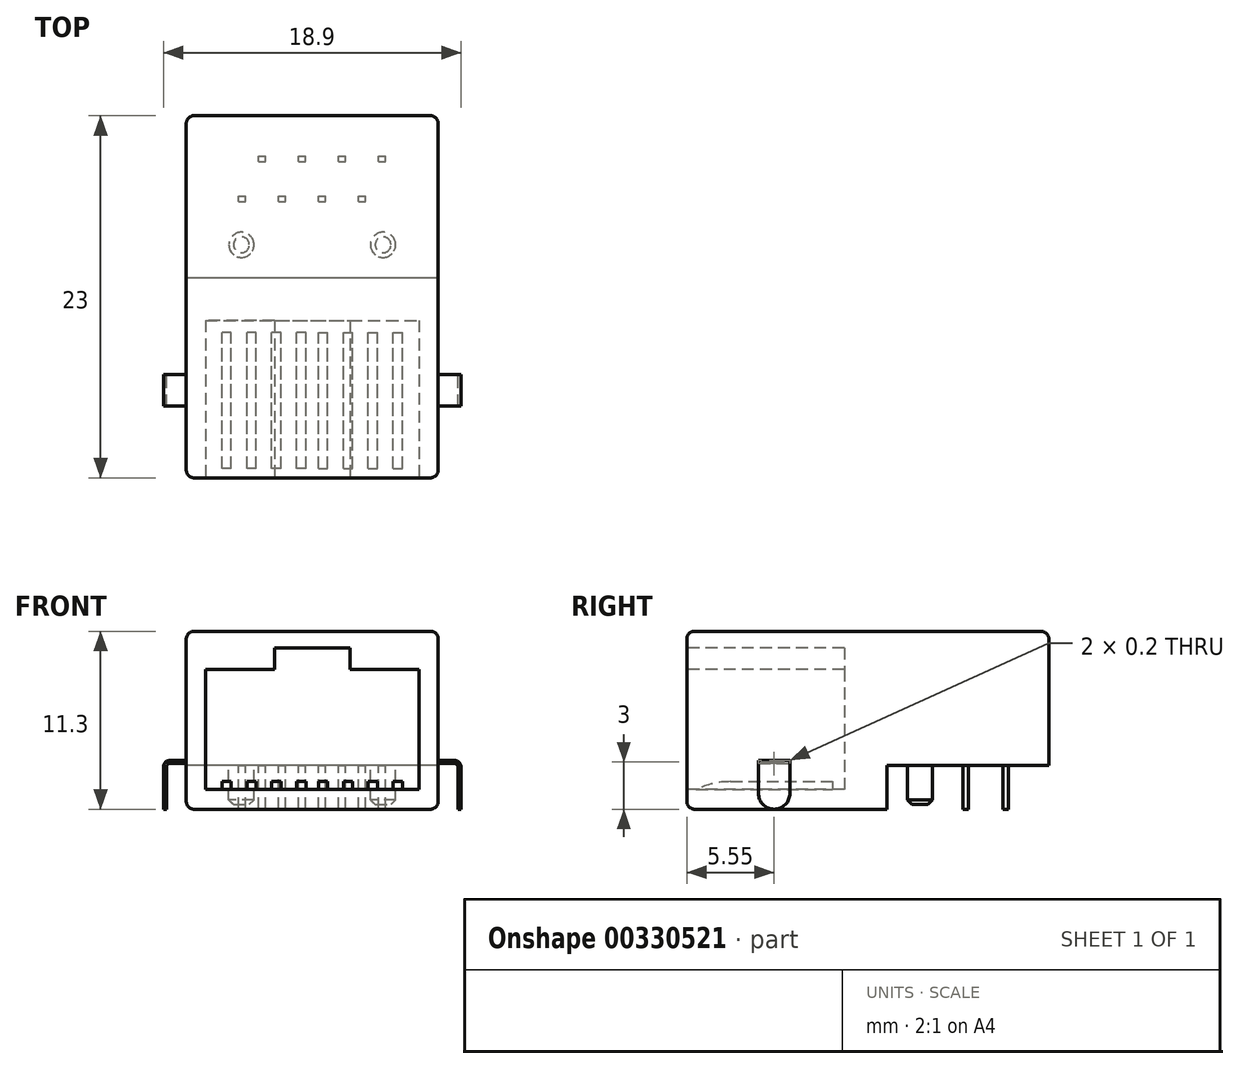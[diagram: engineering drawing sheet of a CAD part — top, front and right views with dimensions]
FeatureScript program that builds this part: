
annotation { "Feature Type Name" : "Feature", "Feature Type Description" : "" }
export const myFeature = defineFeature(function(context is Context, id is Id, definition is map)
    precondition{}
    {
        {
            var Q0;
            Q0=qCreatedBy(makeId("Top.planeOp"),FACE);
            var sketch = newSketch(context, id + "F0", { "sketchPlane" : qUnion([Q0])});
            skLineSegment(sketch, "E0.bottom", {"start": v(8, -11.5) * mm, "end": v(-8, -11.5) * mm});
            skLineSegment(sketch, "E0.top", {"start": v(8, 11.5) * mm, "end": v(-8, 11.5) * mm});
            skLineSegment(sketch, "E0.left", {"start": v(8, -11.5) * mm, "end": v(8, 11.5) * mm});
            skLineSegment(sketch, "E0.right", {"start": v(-8, -11.5) * mm, "end": v(-8, 11.5) * mm});
            skPoint(sketch, "E0.middle", {"position": v(0, 0) * mm});
            skSolve(sketch);
        }
        {
            var Q0;
            Q0 = qSketchRegion(id + "F0", true);
            extrude(context, id + "F1", {"entities" : qUnion([Q0]), "depth" : 8.5 * mm, "offsetDistance" : 25 * mm});
        }
        {
            var Q0;
            Q0=makeQuery(id+"F1.opExtrude","CAP_FACE",FACE,{"disambiguationData":[OSD([sQuery(id+"F0.wireOp",EDGE,"E0.bottom"),sQuery(id+"F0.wireOp",EDGE,"E0.top"),sQuery(id+"F0.wireOp",EDGE,"E0.left"),sQuery(id+"F0.wireOp",EDGE,"E0.right")])],"isStart":true});
            var sketch = newSketch(context, id + "F2", { "sketchPlane" : qUnion([Q0])});
            skLineSegment(sketch, "E1.bottom", {"start": v(8, 11.5) * mm, "end": v(-8, 11.5) * mm});
            skLineSegment(sketch, "E1.top", {"start": v(8, -1.2) * mm, "end": v(-8, -1.2) * mm});
            skLineSegment(sketch, "E1.left", {"start": v(8, 11.5) * mm, "end": v(8, -1.2) * mm});
            skLineSegment(sketch, "E1.right", {"start": v(-8, 11.5) * mm, "end": v(-8, -1.2) * mm});
            skSolve(sketch);
        }
        {
            var Q0;
            Q0=makeQuery(id+"F2.imprint","IMPRINT",FACE,{"disambiguationData":[TD([[makeQuery(id+"F2.imprint","IMPRINT",EDGE,{"derivedFrom":sQuery(id+"F2.wireOp",EDGE,"E1.bottom")}),1.0]])]});
            extrude(context, id + "F3", {"entities" : qUnion([Q0]), "operationType" : NewBodyOperationType.ADD, "depth" : (11.3 - 8.5) * mm, "offsetDistance" : 25 * mm});
        }
        {
            var Q0;
            Q0=makeQuery(id+"F3.boolean.opBoolean","MERGE",EDGE,{"derivedFrom":[makeQuery(id+"F1.opExtrude","SWEPT_EDGE",EDGE,{"disambiguationData":[OSD([sQuery(id+"F0.wireOp",EDGE,"E0.bottom"),sQuery(id+"F0.wireOp",EDGE,"E0.right")])]}),makeQuery(id+"F3.opExtrude","SWEPT_EDGE",EDGE,{"disambiguationData":[OSD([sQuery(id+"F2.wireOp",EDGE,"E1.bottom"),sQuery(id+"F2.wireOp",EDGE,"E1.right")])]})]});
            var Q1;
            Q1=makeQuery(id+"F3.boolean.opBoolean","MERGE",EDGE,{"derivedFrom":[makeQuery(id+"F1.opExtrude","SWEPT_EDGE",EDGE,{"disambiguationData":[OSD([sQuery(id+"F0.wireOp",EDGE,"E0.bottom"),sQuery(id+"F0.wireOp",EDGE,"E0.left")])]}),makeQuery(id+"F3.opExtrude","SWEPT_EDGE",EDGE,{"disambiguationData":[OSD([sQuery(id+"F2.wireOp",EDGE,"E1.bottom"),sQuery(id+"F2.wireOp",EDGE,"E1.left")])]})]});
            var Q2;
            Q2=makeQuery(id+"F1.opExtrude","SWEPT_EDGE",EDGE,{"disambiguationData":[OSD([sQuery(id+"F0.wireOp",EDGE,"E0.top"),sQuery(id+"F0.wireOp",EDGE,"E0.left")])]});
            var Q3;
            Q3=makeQuery(id+"F1.opExtrude","SWEPT_EDGE",EDGE,{"disambiguationData":[OSD([sQuery(id+"F0.wireOp",EDGE,"E0.top"),sQuery(id+"F0.wireOp",EDGE,"E0.right")])]});
            var Q4;
            Q4=makeQuery(id+"F1.opExtrude","CAP_EDGE",EDGE,{"disambiguationData":[OSD([sQuery(id+"F0.wireOp",EDGE,"E0.bottom")])],"isStart":false});
            var Q5;
            Q5=makeQuery(id+"F1.opExtrude","CAP_EDGE",EDGE,{"disambiguationData":[OSD([sQuery(id+"F0.wireOp",EDGE,"E0.right")])],"isStart":false});
            var Q6;
            Q6=makeQuery(id+"F1.opExtrude","CAP_EDGE",EDGE,{"disambiguationData":[OSD([sQuery(id+"F0.wireOp",EDGE,"E0.top")])],"isStart":false});
            var Q7;
            Q7=makeQuery(id+"F1.opExtrude","CAP_EDGE",EDGE,{"disambiguationData":[OSD([sQuery(id+"F0.wireOp",EDGE,"E0.left")])],"isStart":false});
            var Q8;
            Q8=makeQuery(id+"F3.opExtrude","CAP_EDGE",EDGE,{"disambiguationData":[OSD([sQuery(id+"F2.wireOp",EDGE,"E1.bottom")])],"isStart":false});
            var Q9;
            Q9=makeQuery(id+"F3.opExtrude","CAP_EDGE",EDGE,{"disambiguationData":[OSD([sQuery(id+"F2.wireOp",EDGE,"E1.right")])],"isStart":false});
            var Q10;
            Q10=makeQuery(id+"F3.opExtrude","CAP_EDGE",EDGE,{"disambiguationData":[OSD([sQuery(id+"F2.wireOp",EDGE,"E1.left")])],"isStart":false});
            fillet(context, id + "F4", {"entities" : qUnion([Q0, Q1, Q2, Q3, Q4, Q5, Q6, Q7, Q8, Q9, Q10]), "radius" : .5 * mm, "tangentPropagation" : true, "allowEdgeOverflow" : false});
        }
        {
            var Q0;
            Q0=makeQuery(id+"F1.opExtrude","CAP_FACE",FACE,{"disambiguationData":[OSD([sQuery(id+"F0.wireOp",EDGE,"E0.bottom"),sQuery(id+"F0.wireOp",EDGE,"E0.top"),sQuery(id+"F0.wireOp",EDGE,"E0.left"),sQuery(id+"F0.wireOp",EDGE,"E0.right")])],"isStart":true});
            var sketch = newSketch(context, id + "F5", { "sketchPlane" : qUnion([Q0])});
            skCircle(sketch, "E2", {"center": v(4.5, -3.3) * mm, "radius": 0.8 * mm});
            skLineSegment(sketch, "E3", {"start": v(0, -11.5) * mm, "end": v(0, 9.2) * mm, "construction": true});
            skCircle(sketch, "E4.MirrorC", {"center": v(-4.5, -3.3) * mm, "radius": 0.8 * mm});
            skSolve(sketch);
        }
        {
            var Q0;
            Q0 = qSketchRegion(id + "F5", true);
            extrude(context, id + "F6", {"entities" : qUnion([Q0]), "operationType" : NewBodyOperationType.ADD, "depth" : 2.5 * mm, "offsetDistance" : 25 * mm});
        }
        {
            var Q0;
            Q0=makeQuery(id+"F6.opExtrude","CAP_EDGE",EDGE,{"disambiguationData":[OSD([sQuery(id+"F5.wireOp",EDGE,"E2")])],"isStart":false});
            var Q1;
            Q1=makeQuery(id+"F6.opExtrude","CAP_EDGE",EDGE,{"disambiguationData":[OSD([sQuery(id+"F5.wireOp",EDGE,"E4.MirrorC")])],"isStart":false});
            chamfer(context, id + "F7", {"entities" : qUnion([Q0, Q1]), "width" : .3 * mm, "tangentPropagation" : true});
        }
        {
            var Q0;
            Q0=makeQuery(id+"F3.boolean.opBoolean","MERGE",FACE,{"derivedFrom":[makeQuery(id+"F1.opExtrude","SWEPT_FACE",FACE,{"disambiguationData":[OSD([sQuery(id+"F0.wireOp",EDGE,"E0.bottom")])]}),makeQuery(id+"F3.opExtrude","SWEPT_FACE",FACE,{"disambiguationData":[OSD([sQuery(id+"F2.wireOp",EDGE,"E1.bottom")])]})]});
            var sketch = newSketch(context, id + "F8", { "sketchPlane" : qUnion([Q0])});
            skLineSegment(sketch, "E5", {"start": v(0, 8) * mm, "end": v(0, -2.3) * mm, "construction": true});
            skLineSegment(sketch, "E6", {"start": v(0, 7.46) * mm, "end": v(2.4, 7.46) * mm});
            skLineSegment(sketch, "E7", {"start": v(2.4, 7.46) * mm, "end": v(2.4, 6.09) * mm});
            skLineSegment(sketch, "E8", {"start": v(2.4, 6.09) * mm, "end": v(6.78, 6.09) * mm});
            skLineSegment(sketch, "E9", {"start": v(6.78, 6.09) * mm, "end": v(6.78, -1.54) * mm});
            skLineSegment(sketch, "E10", {"start": v(6.78, -1.54) * mm, "end": v(0, -1.54) * mm});
            skLineSegment(sketch, "E11.MirrorCS", {"start": v(-6.78, -1.54) * mm, "end": v(0, -1.54) * mm});
            skLineSegment(sketch, "E12.MirrorCS", {"start": v(-6.78, 6.09) * mm, "end": v(-6.78, -1.54) * mm});
            skLineSegment(sketch, "E13.MirrorCS", {"start": v(-2.4, 6.09) * mm, "end": v(-6.78, 6.09) * mm});
            skLineSegment(sketch, "E14.MirrorCS", {"start": v(0, 7.46) * mm, "end": v(-2.4, 7.46) * mm});
            skLineSegment(sketch, "E15.MirrorCS", {"start": v(-2.4, 7.46) * mm, "end": v(-2.4, 6.09) * mm});
            skSolve(sketch);
        }
        {
            var Q0;
            Q0 = qSketchRegion(id + "F8", true);
            extrude(context, id + "F9", {"entities" : qUnion([Q0]), "operationType" : NewBodyOperationType.REMOVE, "oppositeDirection" : true, "depth" : 10 * mm, "offsetDistance" : 25 * mm});
        }
        {
            var Q0;
            Q0=makeQuery(id+"F9.boolean.opBoolean","COPY",FACE,{"derivedFrom":makeQuery(id+"F9.opExtrude","SWEPT_FACE",FACE,{"disambiguationData":[OSD([sQuery(id+"F8.wireOp",EDGE,"E10"),sQuery(id+"F8.wireOp",EDGE,"E11.MirrorCS")])]})});
            var sketch = newSketch(context, id + "F10", { "sketchPlane" : qUnion([Q0])});
            skLineSegment(sketch, "E16", {"start": v(0, -11.5) * mm, "end": v(0, -1.5) * mm, "construction": true});
            skLineSegment(sketch, "E17.bottom", {"start": v(0.4, -10.9) * mm, "end": v(0.99, -10.9) * mm});
            skLineSegment(sketch, "E17.top", {"start": v(0.4, -2.26) * mm, "end": v(0.99, -2.26) * mm});
            skLineSegment(sketch, "E17.left", {"start": v(0.4, -10.9) * mm, "end": v(0.4, -2.26) * mm});
            skLineSegment(sketch, "E17.right", {"start": v(0.99, -10.9) * mm, "end": v(0.99, -2.26) * mm});
            skLineSegment(sketch, "E18.1.0.0", {"start": v(1.98, -10.9) * mm, "end": v(2.57, -10.9) * mm});
            skLineSegment(sketch, "E18.1.0.1", {"start": v(1.98, -2.26) * mm, "end": v(2.57, -2.26) * mm});
            skLineSegment(sketch, "E18.1.0.2", {"start": v(1.98, -10.9) * mm, "end": v(1.98, -2.26) * mm});
            skLineSegment(sketch, "E18.1.0.3", {"start": v(2.57, -10.9) * mm, "end": v(2.57, -2.26) * mm});
            skLineSegment(sketch, "E18.2.0.0", {"start": v(3.56, -10.9) * mm, "end": v(4.15, -10.9) * mm});
            skLineSegment(sketch, "E18.2.0.1", {"start": v(3.56, -2.26) * mm, "end": v(4.15, -2.26) * mm});
            skLineSegment(sketch, "E18.2.0.2", {"start": v(3.56, -10.9) * mm, "end": v(3.56, -2.26) * mm});
            skLineSegment(sketch, "E18.2.0.3", {"start": v(4.15, -10.9) * mm, "end": v(4.15, -2.26) * mm});
            skLineSegment(sketch, "E18.3.0.0", {"start": v(5.14, -10.9) * mm, "end": v(5.73, -10.9) * mm});
            skLineSegment(sketch, "E18.3.0.1", {"start": v(5.14, -2.26) * mm, "end": v(5.73, -2.26) * mm});
            skLineSegment(sketch, "E18.3.0.2", {"start": v(5.14, -10.9) * mm, "end": v(5.14, -2.26) * mm});
            skLineSegment(sketch, "E18.3.0.3", {"start": v(5.73, -10.9) * mm, "end": v(5.73, -2.26) * mm});
            skLineSegment(sketch, "E18.direction1", {"start": v(0.4, -10.9) * mm, "end": v(1.98, -10.9) * mm, "construction": true});
            skLineSegment(sketch, "E19.MirrorCS", {"start": v(-0.4, -10.9) * mm, "end": v(-0.99, -10.9) * mm});
            skLineSegment(sketch, "E20.MirrorCS", {"start": v(-4.15, -10.9) * mm, "end": v(-4.15, -2.26) * mm});
            skLineSegment(sketch, "E21.MirrorCS", {"start": v(-3.56, -10.9) * mm, "end": v(-3.56, -2.26) * mm});
            skLineSegment(sketch, "E22.MirrorCS", {"start": v(-3.56, -2.26) * mm, "end": v(-4.15, -2.26) * mm});
            skLineSegment(sketch, "E23.MirrorCS", {"start": v(-3.56, -10.9) * mm, "end": v(-4.15, -10.9) * mm});
            skLineSegment(sketch, "E24.MirrorCS", {"start": v(-2.57, -10.9) * mm, "end": v(-2.57, -2.26) * mm});
            skLineSegment(sketch, "E25.MirrorCS", {"start": v(-1.98, -10.9) * mm, "end": v(-1.98, -2.26) * mm});
            skLineSegment(sketch, "E26.MirrorCS", {"start": v(-1.98, -2.26) * mm, "end": v(-2.57, -2.26) * mm});
            skLineSegment(sketch, "E27.MirrorCS", {"start": v(-1.98, -10.9) * mm, "end": v(-2.57, -10.9) * mm});
            skLineSegment(sketch, "E28.MirrorCS", {"start": v(-0.99, -10.9) * mm, "end": v(-0.99, -2.26) * mm});
            skLineSegment(sketch, "E29.MirrorCS", {"start": v(-0.4, -10.9) * mm, "end": v(-0.4, -2.26) * mm});
            skLineSegment(sketch, "E30.MirrorCS", {"start": v(-0.4, -2.26) * mm, "end": v(-0.99, -2.26) * mm});
            skLineSegment(sketch, "E31.MirrorCS", {"start": v(-5.73, -10.9) * mm, "end": v(-5.73, -2.26) * mm});
            skLineSegment(sketch, "E32.MirrorCS", {"start": v(-5.14, -10.9) * mm, "end": v(-5.14, -2.26) * mm});
            skLineSegment(sketch, "E33.MirrorCS", {"start": v(-5.14, -2.26) * mm, "end": v(-5.73, -2.26) * mm});
            skLineSegment(sketch, "E34.MirrorCS", {"start": v(-0.4, -10.9) * mm, "end": v(-1.98, -10.9) * mm, "construction": true});
            skLineSegment(sketch, "E35.MirrorCS", {"start": v(-5.14, -10.9) * mm, "end": v(-5.73, -10.9) * mm});
            skSolve(sketch);
        }
        {
            var Q0;
            Q0 = qSketchRegion(id + "F10", true);
            extrude(context, id + "F11", {"entities" : qUnion([Q0]), "depth" : .5 * mm, "offsetDistance" : 25 * mm});
        }
        {
            var Q0;
            Q0=makeQuery(id+"F11.opExtrude","CAP_EDGE",EDGE,{"disambiguationData":[OSD([sQuery(id+"F10.wireOp",EDGE,"E35.MirrorCS")])],"isStart":false});
            var Q1;
            Q1=makeQuery(id+"F11.opExtrude","CAP_EDGE",EDGE,{"disambiguationData":[OSD([sQuery(id+"F10.wireOp",EDGE,"E23.MirrorCS")])],"isStart":false});
            var Q2;
            Q2=makeQuery(id+"F11.opExtrude","CAP_EDGE",EDGE,{"disambiguationData":[OSD([sQuery(id+"F10.wireOp",EDGE,"E27.MirrorCS")])],"isStart":false});
            var Q3;
            Q3=makeQuery(id+"F11.opExtrude","CAP_EDGE",EDGE,{"disambiguationData":[OSD([sQuery(id+"F10.wireOp",EDGE,"E19.MirrorCS")])],"isStart":false});
            var Q4;
            Q4=makeQuery(id+"F11.opExtrude","CAP_EDGE",EDGE,{"disambiguationData":[OSD([sQuery(id+"F10.wireOp",EDGE,"E17.bottom")])],"isStart":false});
            var Q5;
            Q5=makeQuery(id+"F11.opExtrude","CAP_EDGE",EDGE,{"disambiguationData":[OSD([sQuery(id+"F10.wireOp",EDGE,"E18.1.0.0")])],"isStart":false});
            var Q6;
            Q6=makeQuery(id+"F11.opExtrude","CAP_EDGE",EDGE,{"disambiguationData":[OSD([sQuery(id+"F10.wireOp",EDGE,"E18.2.0.0")])],"isStart":false});
            var Q7;
            Q7=makeQuery(id+"F11.opExtrude","CAP_EDGE",EDGE,{"disambiguationData":[OSD([sQuery(id+"F10.wireOp",EDGE,"E18.3.0.0")])],"isStart":false});
            fillet(context, id + "F12", {"entities" : qUnion([Q0, Q1, Q2, Q3, Q4, Q5, Q6, Q7]), "radius" : 5 * mm, "tangentPropagation" : true, "allowEdgeOverflow" : false});
        }
        {
            var Q0;
            Q0=makeQuery(id+"F1.opExtrude","CAP_FACE",FACE,{"disambiguationData":[OSD([sQuery(id+"F0.wireOp",EDGE,"E0.bottom"),sQuery(id+"F0.wireOp",EDGE,"E0.top"),sQuery(id+"F0.wireOp",EDGE,"E0.left"),sQuery(id+"F0.wireOp",EDGE,"E0.right")])],"isStart":true});
            var sketch = newSketch(context, id + "F13", { "sketchPlane" : qUnion([Q0])});
            skLineSegment(sketch, "E36", {"start": v(0, -1.2) * mm, "end": v(0, -11.5) * mm, "construction": true});
            skLineSegment(sketch, "E37", {"start": v(6.92, -8.76) * mm, "end": v(-6.94, -8.76) * mm, "construction": true});
            skLineSegment(sketch, "E38", {"start": v(6.71, -6.22) * mm, "end": v(-6.94, -6.22) * mm, "construction": true});
            skLineSegment(sketch, "E39", {"start": v(4.5, -3.3) * mm, "end": v(-4.5, -3.3) * mm, "construction": true});
            skLineSegment(sketch, "E40.bottom", {"start": v(4.22, -8.59) * mm, "end": v(4.67, -8.59) * mm});
            skLineSegment(sketch, "E40.top", {"start": v(4.22, -8.94) * mm, "end": v(4.67, -8.94) * mm});
            skLineSegment(sketch, "E40.left", {"start": v(4.22, -8.59) * mm, "end": v(4.22, -8.94) * mm});
            skLineSegment(sketch, "E40.right", {"start": v(4.67, -8.59) * mm, "end": v(4.67, -8.94) * mm});
            skPoint(sketch, "E40.middle", {"position": v(4.45, -8.76) * mm});
            skLineSegment(sketch, "E41.1.0.0", {"start": v(2.13, -8.59) * mm, "end": v(2.13, -8.94) * mm});
            skLineSegment(sketch, "E41.1.0.1", {"start": v(1.68, -8.59) * mm, "end": v(1.68, -8.94) * mm});
            skLineSegment(sketch, "E41.1.0.2", {"start": v(1.68, -8.94) * mm, "end": v(2.13, -8.94) * mm});
            skLineSegment(sketch, "E41.1.0.3", {"start": v(1.68, -8.59) * mm, "end": v(2.13, -8.59) * mm});
            skPoint(sketch, "E41.1.0.4", {"position": v(1.9, -8.76) * mm});
            skLineSegment(sketch, "E41.2.0.0", {"start": v(-0.4, -8.59) * mm, "end": v(-0.4, -8.94) * mm});
            skLineSegment(sketch, "E41.2.0.1", {"start": v(-0.86, -8.59) * mm, "end": v(-0.86, -8.94) * mm});
            skLineSegment(sketch, "E41.2.0.2", {"start": v(-0.86, -8.94) * mm, "end": v(-0.4, -8.94) * mm});
            skLineSegment(sketch, "E41.2.0.3", {"start": v(-0.86, -8.59) * mm, "end": v(-0.4, -8.59) * mm});
            skPoint(sketch, "E41.2.0.4", {"position": v(-0.64, -8.76) * mm});
            skLineSegment(sketch, "E41.3.0.0", {"start": v(-2.95, -8.59) * mm, "end": v(-2.95, -8.94) * mm});
            skLineSegment(sketch, "E41.3.0.1", {"start": v(-3.4, -8.59) * mm, "end": v(-3.4, -8.94) * mm});
            skLineSegment(sketch, "E41.3.0.2", {"start": v(-3.4, -8.94) * mm, "end": v(-2.95, -8.94) * mm});
            skLineSegment(sketch, "E41.3.0.3", {"start": v(-3.4, -8.59) * mm, "end": v(-2.95, -8.59) * mm});
            skPoint(sketch, "E41.3.0.4", {"position": v(-3.17, -8.76) * mm});
            skLineSegment(sketch, "E41.direction1", {"start": v(4.22, -8.94) * mm, "end": v(1.68, -8.94) * mm, "construction": true});
            skLineSegment(sketch, "E42.bottom", {"start": v(2.95, -6.05) * mm, "end": v(3.4, -6.05) * mm});
            skLineSegment(sketch, "E42.top", {"start": v(2.95, -6.4) * mm, "end": v(3.4, -6.4) * mm});
            skLineSegment(sketch, "E42.left", {"start": v(2.95, -6.05) * mm, "end": v(2.95, -6.4) * mm});
            skLineSegment(sketch, "E42.right", {"start": v(3.4, -6.05) * mm, "end": v(3.4, -6.4) * mm});
            skPoint(sketch, "E42.middle", {"position": v(3.17, -6.22) * mm});
            skLineSegment(sketch, "E43.1.0.0", {"start": v(0.4, -6.4) * mm, "end": v(0.86, -6.4) * mm});
            skLineSegment(sketch, "E43.1.0.1", {"start": v(0.4, -6.05) * mm, "end": v(0.4, -6.4) * mm});
            skLineSegment(sketch, "E43.1.0.2", {"start": v(0.4, -6.05) * mm, "end": v(0.86, -6.05) * mm});
            skLineSegment(sketch, "E43.1.0.3", {"start": v(4.17, -6.22) * mm, "end": v(-9.48, -6.22) * mm, "construction": true});
            skLineSegment(sketch, "E43.1.0.4", {"start": v(0.86, -6.05) * mm, "end": v(0.86, -6.4) * mm});
            skPoint(sketch, "E43.1.0.5", {"position": v(0.63, -6.22) * mm});
            skLineSegment(sketch, "E43.2.0.0", {"start": v(-2.13, -6.4) * mm, "end": v(-1.68, -6.4) * mm});
            skLineSegment(sketch, "E43.2.0.1", {"start": v(-2.13, -6.05) * mm, "end": v(-2.13, -6.4) * mm});
            skLineSegment(sketch, "E43.2.0.2", {"start": v(-2.13, -6.05) * mm, "end": v(-1.68, -6.05) * mm});
            skLineSegment(sketch, "E43.2.0.3", {"start": v(1.63, -6.22) * mm, "end": v(-12.02, -6.22) * mm, "construction": true});
            skLineSegment(sketch, "E43.2.0.4", {"start": v(-1.68, -6.05) * mm, "end": v(-1.68, -6.4) * mm});
            skPoint(sketch, "E43.2.0.5", {"position": v(-1.9, -6.22) * mm});
            skLineSegment(sketch, "E43.3.0.0", {"start": v(-4.67, -6.4) * mm, "end": v(-4.22, -6.4) * mm});
            skLineSegment(sketch, "E43.3.0.1", {"start": v(-4.67, -6.05) * mm, "end": v(-4.67, -6.4) * mm});
            skLineSegment(sketch, "E43.3.0.2", {"start": v(-4.67, -6.05) * mm, "end": v(-4.22, -6.05) * mm});
            skLineSegment(sketch, "E43.3.0.3", {"start": v(-0.9, -6.22) * mm, "end": v(-14.56, -6.22) * mm, "construction": true});
            skLineSegment(sketch, "E43.3.0.4", {"start": v(-4.22, -6.05) * mm, "end": v(-4.22, -6.4) * mm});
            skPoint(sketch, "E43.3.0.5", {"position": v(-4.45, -6.22) * mm});
            skLineSegment(sketch, "E43.direction1", {"start": v(-6.94, -6.22) * mm, "end": v(-9.48, -6.22) * mm, "construction": true});
            skSolve(sketch);
        }
        {
            var Q0;
            Q0 = qSketchRegion(id + "F13", true);
            extrude(context, id + "F14", {"entities" : qUnion([Q0]), "operationType" : NewBodyOperationType.ADD, "depth" : (11.3 - 8.5) * mm, "offsetDistance" : 25 * mm});
        }
        {
            var Q0;
            Q0=makeQuery(id+"F3.boolean.opBoolean","MERGE",FACE,{"derivedFrom":[makeQuery(id+"F1.opExtrude","SWEPT_FACE",FACE,{"disambiguationData":[OSD([sQuery(id+"F0.wireOp",EDGE,"E0.bottom")])]}),makeQuery(id+"F3.opExtrude","SWEPT_FACE",FACE,{"disambiguationData":[OSD([sQuery(id+"F2.wireOp",EDGE,"E1.bottom")])]})]});
            cPlane(context, id + "F15", {"entities" : qUnion([Q0]), "cplaneType" : CPlaneType.OFFSET, "offset" : 5.55 * mm, "oppositeDirection" : true, "width" : 150 * mm, "height" : 150 * mm});
        }
        {
            var Q0;
            Q0=qCreatedBy(id+"F15.planeOp",FACE);
            var sketch = newSketch(context, id + "F16", { "sketchPlane" : qUnion([Q0])});
            skLineSegment(sketch, "E44", {"start": v(0, -4.17) * mm, "end": v(0, 3.07) * mm, "construction": true});
            skLineSegment(sketch, "E45", {"start": v(9.35, -4.17) * mm, "end": v(9.35, 3.17) * mm, "construction": true});
            skLineSegment(sketch, "E46", {"start": v(8, 0.3) * mm, "end": v(8, 0.1) * mm});
            skLineSegment(sketch, "E47", {"start": v(9.45, -2.8) * mm, "end": v(9.45, -0.1) * mm});
            skLineSegment(sketch, "E48", {"start": v(9.05, 0.3) * mm, "end": v(8, 0.3) * mm});
            skPoint(sketch, "E49.visualSharp", {"position": v(9.45, 0) * mm});
            skArc(sketch, "E49.filletArc", {"start": v(9.45, -0.1) * mm, "mid": v(9.33, 0.2) * mm, "end": v(9.05, 0.3) * mm});
            skArc(sketch, "E50.0", {"start": v(9.25, -0.1) * mm, "mid": v(9.2, 0.05) * mm, "end": v(9.05, 0.1) * mm});
            skLineSegment(sketch, "E51", {"start": v(9.05, 0.1) * mm, "end": v(8, 0.1) * mm});
            skLineSegment(sketch, "E52", {"start": v(9.25, -2.8) * mm, "end": v(9.45, -2.8) * mm});
            skLineSegment(sketch, "E53", {"start": v(9.25, -0.1) * mm, "end": v(9.25, -2.8) * mm});
            skPoint(sketch, "E54.orphan", {"position": v(7.5, -2.8) * mm});
            skPoint(sketch, "E55.orphan", {"position": v(8, -2.3) * mm});
            skPoint(sketch, "E56.orphan", {"position": v(8, 8) * mm});
            skPoint(sketch, "E57.start.orphan", {"position": v(-7.5, -2.8) * mm});
            skLineSegment(sketch, "E58.MirrorCS", {"start": v(-9.25, -2.8) * mm, "end": v(-9.45, -2.8) * mm});
            skLineSegment(sketch, "E59.MirrorCS", {"start": v(-8, 0.3) * mm, "end": v(-8, 0.1) * mm});
            skArc(sketch, "E60.MirrorCS", {"start": v(-9.25, -0.1) * mm, "mid": v(-9.2, 0.05) * mm, "end": v(-9.05, 0.1) * mm});
            skLineSegment(sketch, "E61.MirrorCS", {"start": v(-9.05, 0.3) * mm, "end": v(-8, 0.3) * mm});
            skArc(sketch, "E62.MirrorCS", {"start": v(-9.45, -0.1) * mm, "mid": v(-9.33, 0.2) * mm, "end": v(-9.05, 0.3) * mm});
            skPoint(sketch, "E63.MirrorP", {"position": v(-8, -2.3) * mm});
            skLineSegment(sketch, "E64.MirrorCS", {"start": v(-9.25, -0.1) * mm, "end": v(-9.25, -2.8) * mm});
            skLineSegment(sketch, "E65.MirrorCS", {"start": v(-9.05, 0.1) * mm, "end": v(-8, 0.1) * mm});
            skLineSegment(sketch, "E66.MirrorCS", {"start": v(-9.45, -2.8) * mm, "end": v(-9.45, -0.1) * mm});
            skPoint(sketch, "E67.MirrorP", {"position": v(-9.45, 0) * mm});
            skLineSegment(sketch, "E68.MirrorCS", {"start": v(-9.35, -4.17) * mm, "end": v(-9.35, 3.17) * mm, "construction": true});
            skSolve(sketch);
        }
        {
            var Q0;
            Q0 = qSketchRegion(id + "F16", true);
            extrude(context, id + "F17", {"entities" : qUnion([Q0]), "operationType" : NewBodyOperationType.ADD, "depth" : 1 * mm, "offsetDistance" : 25 * mm, "hasSecondDirection" : true, "secondDirectionOppositeDirection" : true, "secondDirectionDepth" : 1 * mm});
        }
        {
            var Q0;
            Q0=makeQuery(id+"F17.opExtrude","CAP_EDGE",EDGE,{"disambiguationData":[OSD([sQuery(id+"F16.wireOp",EDGE,"E52")])],"isStart":false});
            var Q1;
            Q1=makeQuery(id+"F17.opExtrude","CAP_EDGE",EDGE,{"disambiguationData":[OSD([sQuery(id+"F16.wireOp",EDGE,"E52")])],"isStart":true});
            var Q2;
            Q2=makeQuery(id+"F17.opExtrude","CAP_EDGE",EDGE,{"disambiguationData":[OSD([sQuery(id+"F16.wireOp",EDGE,"E58.MirrorCS")])],"isStart":false});
            var Q3;
            Q3=makeQuery(id+"F17.opExtrude","CAP_EDGE",EDGE,{"disambiguationData":[OSD([sQuery(id+"F16.wireOp",EDGE,"E58.MirrorCS")])],"isStart":true});
            fillet(context, id + "F18", {"entities" : qUnion([Q0, Q1, Q2, Q3]), "radius" : 1 * mm, "tangentPropagation" : true, "allowEdgeOverflow" : false});
        }
    });
